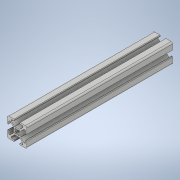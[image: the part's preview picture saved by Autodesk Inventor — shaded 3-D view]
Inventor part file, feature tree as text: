
AUTODESK INVENTOR PART (.ipt)
format: ipt  version: 2022 (Build 260153000, 153)  size: 248,320 bytes
history: native  units: mm
features: extrude x1, sketch x1
ambient origin geometry x8: Origin, YZ Plane, XZ Plane, XY Plane, X Axis, Y Axis, Z Axis, Center Point
bodies: Solid1 (feature_tree)
feature tree (2):
  extrude  "Extrusion1"  Depth=150.0mm
  sketch  "Sketch_1"  dims[d0=150.0mm d1=0.0mm d2=0.5mm d3=0.872665mm d4=0.5mm d5=0.872665mm]
